# Revit family: Mail_Drop-Salsbury_Industries-Private_Access
name_source: partatom
category: Specialty Equipment
revit_build: Autodesk Revit 2016 (Build: 20150714_1515(x64)
units: mm (PartAtom-declared; Revit-internal decimal feet)

## family parameters
Cut with Voids When Loaded = No
Host = Face
OmniClass Number = 23.40.90.14.11
OmniClass Title = Mail Boxes
Part Type = Normal
Room Calculation Point = No
Round Connector Dimension = Use Diameter
Shared = No

## types (2) — shared parameters
Assembly Code = C1030910
Assembly Description = Mailboxes
Default Elevation = 48 "
Deposit Slot Height = 4 "
Deposit Slot Width = 11 "
Depth = 6 "
Height = 7 "
Lock Material = Stainless Steel - Salsbury Finish -  Polished
Manufacturer = Salsbury Industries
MasterFormat Number = 10 55 00
MasterFormat Title = Postal Specialties
OmniClass 23 Number = 23.40.90.14.11
OmniClass 23 Title = Mail Boxes
Receptacle Depth = 7.5 "
Receptacle Height = 19 "
Receptacle Width = 15 "
Rough Opening Height = 5.5 "
Rough Opening Width = 12.25 "
URL = www.mailboxes.com
Version = 1.0 (07/31/19)
Width = 14 "

## per-type parameters (varying)
| type | Description | Including Receptacle | Type Comments |
| 2255 | Recessed Mounted - Private Access (May be used for USPS residential door mail delivery) | No | Mail Drop |
| 2255 with 2256 | Recessed Mounted - Private Access | Yes | Mail Drop with Receptacle |

note: column(s) folded — value = type name in every type: Model

## geometry (parser evidence)
native form markers: Sweep x2
no freeform markers — native parametric forms only
